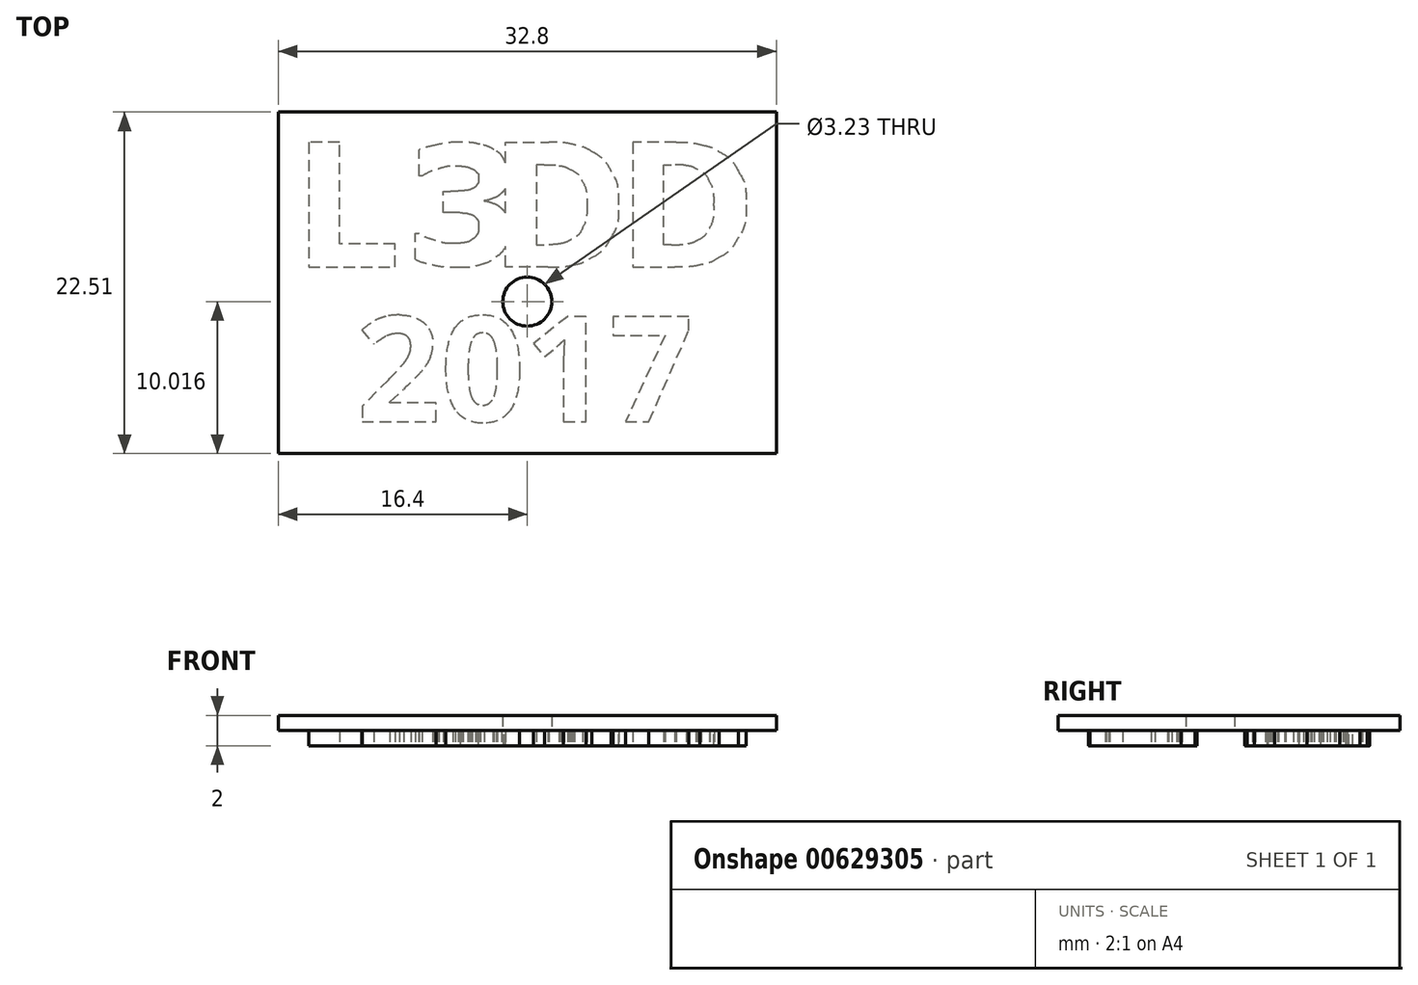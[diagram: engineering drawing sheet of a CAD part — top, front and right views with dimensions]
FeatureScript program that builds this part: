
annotation { "Feature Type Name" : "Feature", "Feature Type Description" : "" }
export const myFeature = defineFeature(function(context is Context, id is Id, definition is map)
    precondition{}
    {
        {
            var Q0;
            Q0=qCreatedBy(makeId("Top.planeOp"),FACE);
            var sketch = newSketch(context, id + "F0", { "sketchPlane" : qUnion([Q0])});
            skText(sketch, "E0", { "text": "2017", "fontName": "OpenSans-Bold.ttf"});
            skFitSpline(sketch, "E1", {"points": [v(-4.44, 4.1) * mm, v(-4.95, 4.1) * mm, v(-5.45, 4.05) * mm, v(-5.95, 3.94) * mm]});
            skFitSpline(sketch, "E2", {"points": [v(-5.95, 3.94) * mm, v(-6.45, 3.84) * mm, v(-6.84, 3.73) * mm, v(-7.13, 3.61) * mm]});
            skFitSpline(sketch, "E3", {"points": [v(-6.94, 1.9) * mm, v(-6.57, 2.11) * mm, v(-6.2, 2.28) * mm, v(-5.8, 2.4) * mm]});
            skFitSpline(sketch, "E4", {"points": [v(-5.8, 2.4) * mm, v(-5.42, 2.5) * mm, v(-5.06, 2.57) * mm, v(-4.73, 2.57) * mm]});
            skFitSpline(sketch, "E5", {"points": [v(-4.73, 2.57) * mm, v(-4.6, 2.57) * mm, v(-4.43, 2.56) * mm, v(-4.25, 2.54) * mm]});
            skFitSpline(sketch, "E6", {"points": [v(-4.25, 2.54) * mm, v(-4.06, 2.51) * mm, v(-3.95, 2.5) * mm, v(-3.76, 2.42) * mm]});
            skFitSpline(sketch, "E7", {"points": [v(-3.76, 2.42) * mm, v(-3.63, 2.36) * mm, v(-3.5, 2.31) * mm, v(-3.42, 2.22) * mm]});
            skFitSpline(sketch, "E8", {"points": [v(-3.42, 2.22) * mm, v(-3.3, 2.12) * mm, v(-3.21, 2.03) * mm, v(-3.21, 1.8) * mm]});
            skFitSpline(sketch, "E9", {"points": [v(-3.21, 1.8) * mm, v(-3.21, 1.48) * mm, v(-3.25, 1.41) * mm, v(-3.33, 1.3) * mm]});
            skFitSpline(sketch, "E10", {"points": [v(-3.33, 1.3) * mm, v(-3.4, 1.2) * mm, v(-3.52, 1.1) * mm, v(-3.68, 1.04) * mm]});
            skFitSpline(sketch, "E11", {"points": [v(-3.68, 1.04) * mm, v(-3.83, 0.97) * mm, v(-4.12, 0.93) * mm, v(-4.34, 0.91) * mm]});
            skFitSpline(sketch, "E12", {"points": [v(-4.34, 0.91) * mm, v(-4.55, 0.9) * mm, v(-4.8, 0.89) * mm, v(-5.07, 0.89) * mm]});
            skLineSegment(sketch, "E13", {"start": v(-7.13, 3.61) * mm, "end": v(-7.13, 1.9) * mm});
            skLineSegment(sketch, "E14", {"start": v(-7.13, 1.9) * mm, "end": v(-6.94, 1.9) * mm});
            skFitSpline(sketch, "E15", {"points": [v(-5.08, -0.52) * mm, v(-4.87, -0.52) * mm, v(-4.65, -0.53) * mm, v(-4.4, -0.53) * mm]});
            skFitSpline(sketch, "E16", {"points": [v(-4.4, -0.53) * mm, v(-4.16, -0.54) * mm, v(-3.95, -0.57) * mm, v(-3.78, -0.62) * mm]});
            skFitSpline(sketch, "E17", {"points": [v(-3.78, -0.62) * mm, v(-3.6, -0.68) * mm, v(-3.47, -0.77) * mm, v(-3.36, -0.9) * mm]});
            skFitSpline(sketch, "E18", {"points": [v(-3.36, -0.9) * mm, v(-3.25, -1.02) * mm, v(-3.2, -1.2) * mm, v(-3.2, -1.42) * mm]});
            skFitSpline(sketch, "E19", {"points": [v(-3.2, -1.42) * mm, v(-3.2, -1.66) * mm, v(-3.24, -1.84) * mm, v(-3.32, -1.97) * mm]});
            skFitSpline(sketch, "E20", {"points": [v(-3.32, -1.97) * mm, v(-3.4, -2.1) * mm, v(-3.5, -2.2) * mm, v(-3.63, -2.29) * mm]});
            skFitSpline(sketch, "E21", {"points": [v(-3.63, -2.29) * mm, v(-3.8, -2.4) * mm, v(-4, -2.47) * mm, v(-4.24, -2.5) * mm]});
            skFitSpline(sketch, "E22", {"points": [v(-4.24, -2.5) * mm, v(-4.48, -2.54) * mm, v(-4.7, -2.56) * mm, v(-4.9, -2.56) * mm]});
            skFitSpline(sketch, "E23", {"points": [v(-4.9, -2.56) * mm, v(-5.26, -2.56) * mm, v(-5.64, -2.49) * mm, v(-6.07, -2.36) * mm]});
            skFitSpline(sketch, "E24", {"points": [v(-6.07, -2.36) * mm, v(-6.49, -2.22) * mm, v(-6.85, -2.06) * mm, v(-7.15, -1.88) * mm]});
            skLineSegment(sketch, "E25", {"start": v(-5.07, 0.89) * mm, "end": v(-5.52, 0.89) * mm});
            skLineSegment(sketch, "E26", {"start": v(-5.52, 0.89) * mm, "end": v(-5.52, -0.52) * mm});
            skLineSegment(sketch, "E27", {"start": v(-5.52, -0.52) * mm, "end": v(-5.08, -0.52) * mm});
            skFitSpline(sketch, "E28", {"points": [v(-7.36, -3.61) * mm, v(-7.07, -3.74) * mm, v(-6.69, -3.85) * mm, v(-6.22, -3.96) * mm]});
            skFitSpline(sketch, "E29", {"points": [v(-6.22, -3.96) * mm, v(-5.75, -4.06) * mm, v(-5.2, -4.1) * mm, v(-4.54, -4.1) * mm]});
            skFitSpline(sketch, "E30", {"points": [v(-4.54, -4.1) * mm, v(-3.96, -4.1) * mm, v(-3.48, -4.05) * mm, v(-3.08, -3.93) * mm]});
            skFitSpline(sketch, "E31", {"points": [v(-3.08, -3.93) * mm, v(-2.68, -3.81) * mm, v(-2.33, -3.64) * mm, v(-2.03, -3.42) * mm]});
            skFitSpline(sketch, "E32", {"points": [v(-2.03, -3.42) * mm, v(-1.77, -3.23) * mm, v(-1.58, -3) * mm, v(-1.43, -2.73) * mm]});
            skLineSegment(sketch, "E33", {"start": v(-7.15, -1.88) * mm, "end": v(-7.36, -1.88) * mm});
            skLineSegment(sketch, "E34", {"start": v(-7.36, -1.88) * mm, "end": v(-7.36, -3.61) * mm});
            skFitSpline(sketch, "E35", {"points": [v(1.35, -4.1) * mm, v(1.98, -4.1) * mm, v(2.52, -4.06) * mm, v(2.98, -3.97) * mm]});
            skFitSpline(sketch, "E36", {"points": [v(2.98, -3.97) * mm, v(3.44, -3.88) * mm, v(3.86, -3.72) * mm, v(4.25, -3.48) * mm]});
            skFitSpline(sketch, "E37", {"points": [v(4.25, -3.48) * mm, v(4.76, -3.17) * mm, v(5.18, -2.73) * mm, v(5.52, -2.15) * mm]});
            skFitSpline(sketch, "E38", {"points": [v(5.52, -2.15) * mm, v(5.85, -1.56) * mm, v(6.02, -0.74) * mm, v(6.02, 0) * mm]});
            skFitSpline(sketch, "E39", {"points": [v(6.02, 0) * mm, v(6.02, 0.76) * mm, v(5.86, 1.58) * mm, v(5.55, 2.14) * mm]});
            skFitSpline(sketch, "E40", {"points": [v(5.55, 2.14) * mm, v(5.24, 2.7) * mm, v(4.81, 3.16) * mm, v(4.27, 3.49) * mm]});
            skFitSpline(sketch, "E41", {"points": [v(4.27, 3.49) * mm, v(3.95, 3.69) * mm, v(3.56, 3.84) * mm, v(3.1, 3.94) * mm]});
            skFitSpline(sketch, "E42", {"points": [v(3.1, 3.94) * mm, v(2.63, 4.05) * mm, v(2.07, 4.1) * mm, v(1.43, 4.1) * mm]});
            skLineSegment(sketch, "E43", {"start": v(-1.43, -2.73) * mm, "end": v(-1.43, -4.1) * mm});
            skLineSegment(sketch, "E44", {"start": v(-1.43, -4.1) * mm, "end": v(1.35, -4.1) * mm});
            skFitSpline(sketch, "E45", {"points": [v(-1.43, 2.75) * mm, v(-1.47, 2.84) * mm, v(-1.51, 2.93) * mm, v(-1.55, 3) * mm]});
            skFitSpline(sketch, "E46", {"points": [v(-1.55, 3) * mm, v(-1.7, 3.25) * mm, v(-1.91, 3.46) * mm, v(-2.2, 3.63) * mm]});
            skFitSpline(sketch, "E47", {"points": [v(-2.2, 3.63) * mm, v(-2.44, 3.78) * mm, v(-2.75, 3.9) * mm, v(-3.13, 3.98) * mm]});
            skFitSpline(sketch, "E48", {"points": [v(-3.13, 3.98) * mm, v(-3.5, 4.07) * mm, v(-3.94, 4.1) * mm, v(-4.44, 4.1) * mm]});
            skLineSegment(sketch, "E49", {"start": v(1.43, 4.1) * mm, "end": v(-1.43, 4.1) * mm});
            skLineSegment(sketch, "E50", {"start": v(-1.43, 4.1) * mm, "end": v(-1.43, 2.75) * mm});
            skFitSpline(sketch, "E51", {"points": [v(1.12, 2.64) * mm, v(1.55, 2.64) * mm, v(1.88, 2.62) * mm, v(2.1, 2.58) * mm]});
            skFitSpline(sketch, "E52", {"points": [v(2.1, 2.58) * mm, v(2.31, 2.54) * mm, v(2.53, 2.47) * mm, v(2.74, 2.37) * mm]});
            skFitSpline(sketch, "E53", {"points": [v(2.74, 2.37) * mm, v(3.15, 2.16) * mm, v(3.45, 1.87) * mm, v(3.63, 1.5) * mm]});
            skFitSpline(sketch, "E54", {"points": [v(3.63, 1.5) * mm, v(3.82, 1.13) * mm, v(3.92, 0.53) * mm, v(3.92, 0) * mm]});
            skFitSpline(sketch, "E55", {"points": [v(3.92, 0) * mm, v(3.92, -0.51) * mm, v(3.83, -1.12) * mm, v(3.66, -1.47) * mm]});
            skFitSpline(sketch, "E56", {"points": [v(3.66, -1.47) * mm, v(3.49, -1.83) * mm, v(3.21, -2.11) * mm, v(2.84, -2.32) * mm]});
            skFitSpline(sketch, "E57", {"points": [v(2.84, -2.32) * mm, v(2.63, -2.44) * mm, v(2.4, -2.52) * mm, v(2.18, -2.57) * mm]});
            skFitSpline(sketch, "E58", {"points": [v(2.18, -2.57) * mm, v(1.95, -2.6) * mm, v(1.6, -2.63) * mm, v(1.12, -2.63) * mm]});
            skLineSegment(sketch, "E59", {"start": v(0.6, 2.64) * mm, "end": v(1.12, 2.64) * mm});
            skLineSegment(sketch, "E60", {"start": v(1.12, -2.63) * mm, "end": v(0.6, -2.63) * mm});
            skLineSegment(sketch, "E61", {"start": v(0.6, -2.63) * mm, "end": v(0.6, 2.64) * mm});
            skFitSpline(sketch, "E62", {"points": [v(-1.43, -0.54) * mm, v(-1.51, -0.43) * mm, v(-1.6, -0.33) * mm, v(-1.7, -0.25) * mm]});
            skFitSpline(sketch, "E63", {"points": [v(-1.7, -0.25) * mm, v(-1.87, -0.1) * mm, v(-2.05, 0) * mm, v(-2.25, 0.08) * mm]});
            skFitSpline(sketch, "E64", {"points": [v(-2.25, 0.08) * mm, v(-2.45, 0.15) * mm, v(-2.65, 0.2) * mm, v(-2.83, 0.23) * mm]});
            skLineSegment(sketch, "E65", {"start": v(-1.43, 1.06) * mm, "end": v(-1.43, -0.54) * mm});
            skFitSpline(sketch, "E66", {"points": [v(-2.83, 0.3) * mm, v(-2.65, 0.32) * mm, v(-2.45, 0.37) * mm, v(-2.25, 0.45) * mm]});
            skFitSpline(sketch, "E67", {"points": [v(-2.25, 0.45) * mm, v(-2.05, 0.52) * mm, v(-1.87, 0.63) * mm, v(-1.7, 0.77) * mm]});
            skFitSpline(sketch, "E68", {"points": [v(-1.7, 0.77) * mm, v(-1.6, 0.86) * mm, v(-1.51, 0.96) * mm, v(-1.43, 1.06) * mm]});
            skLineSegment(sketch, "E69", {"start": v(-2.83, 0.23) * mm, "end": v(-2.83, 0.3) * mm});
            skFitSpline(sketch, "E70", {"points": [v(14.4, 0) * mm, v(14.4, -0.74) * mm, v(14.23, -1.56) * mm, v(13.9, -2.15) * mm]});
            skFitSpline(sketch, "E71", {"points": [v(13.9, -2.15) * mm, v(13.56, -2.73) * mm, v(13.13, -3.17) * mm, v(12.62, -3.48) * mm]});
            skFitSpline(sketch, "E72", {"points": [v(12.62, -3.48) * mm, v(12.24, -3.72) * mm, v(11.81, -3.88) * mm, v(11.36, -3.97) * mm]});
            skFitSpline(sketch, "E73", {"points": [v(11.36, -3.97) * mm, v(10.9, -4.06) * mm, v(10.35, -4.1) * mm, v(9.72, -4.1) * mm]});
            skFitSpline(sketch, "E74", {"points": [v(9.8, 4.1) * mm, v(10.45, 4.1) * mm, v(11, 4.05) * mm, v(11.47, 3.94) * mm]});
            skFitSpline(sketch, "E75", {"points": [v(11.47, 3.94) * mm, v(11.93, 3.84) * mm, v(12.33, 3.69) * mm, v(12.64, 3.49) * mm]});
            skFitSpline(sketch, "E76", {"points": [v(12.64, 3.49) * mm, v(13.19, 3.16) * mm, v(13.61, 2.7) * mm, v(13.93, 2.14) * mm]});
            skFitSpline(sketch, "E77", {"points": [v(13.93, 2.14) * mm, v(14.24, 1.58) * mm, v(14.4, 0.76) * mm, v(14.4, 0) * mm]});
            skLineSegment(sketch, "E78", {"start": v(9.72, -4.1) * mm, "end": v(6.94, -4.1) * mm});
            skLineSegment(sketch, "E79", {"start": v(6.94, -4.1) * mm, "end": v(6.94, 4.1) * mm});
            skLineSegment(sketch, "E80", {"start": v(6.94, 4.1) * mm, "end": v(9.8, 4.1) * mm});
            skFitSpline(sketch, "E81", {"points": [v(12.3, 0) * mm, v(12.3, 0.53) * mm, v(12.2, 1.13) * mm, v(12, 1.5) * mm]});
            skFitSpline(sketch, "E82", {"points": [v(12, 1.5) * mm, v(11.82, 1.87) * mm, v(11.52, 2.16) * mm, v(11.11, 2.37) * mm]});
            skFitSpline(sketch, "E83", {"points": [v(11.11, 2.37) * mm, v(10.9, 2.47) * mm, v(10.69, 2.54) * mm, v(10.47, 2.58) * mm]});
            skFitSpline(sketch, "E84", {"points": [v(10.47, 2.58) * mm, v(10.26, 2.62) * mm, v(9.93, 2.64) * mm, v(9.5, 2.64) * mm]});
            skFitSpline(sketch, "E85", {"points": [v(9.5, -2.63) * mm, v(9.97, -2.63) * mm, v(10.33, -2.6) * mm, v(10.56, -2.57) * mm]});
            skFitSpline(sketch, "E86", {"points": [v(10.56, -2.57) * mm, v(10.78, -2.52) * mm, v(11, -2.44) * mm, v(11.22, -2.32) * mm]});
            skFitSpline(sketch, "E87", {"points": [v(11.22, -2.32) * mm, v(11.59, -2.11) * mm, v(11.86, -1.83) * mm, v(12.03, -1.47) * mm]});
            skFitSpline(sketch, "E88", {"points": [v(12.03, -1.47) * mm, v(12.2, -1.12) * mm, v(12.3, -0.51) * mm, v(12.3, 0) * mm]});
            skLineSegment(sketch, "E89", {"start": v(9.5, 2.64) * mm, "end": v(8.98, 2.64) * mm});
            skLineSegment(sketch, "E90", {"start": v(8.98, 2.64) * mm, "end": v(8.98, -2.63) * mm});
            skLineSegment(sketch, "E91", {"start": v(8.98, -2.63) * mm, "end": v(9.5, -2.63) * mm});
            skLineSegment(sketch, "E92", {"start": v(-8.7, -4.1) * mm, "end": v(-14.4, -4.1) * mm});
            skLineSegment(sketch, "E93", {"start": v(-14.4, -4.1) * mm, "end": v(-14.4, 4.1) * mm});
            skLineSegment(sketch, "E94", {"start": v(-14.4, 4.1) * mm, "end": v(-12.36, 4.1) * mm});
            skLineSegment(sketch, "E95", {"start": v(-12.36, 4.1) * mm, "end": v(-12.36, -2.58) * mm});
            skLineSegment(sketch, "E96", {"start": v(-12.36, -2.58) * mm, "end": v(-8.7, -2.58) * mm});
            skLineSegment(sketch, "E97", {"start": v(-8.7, -2.58) * mm, "end": v(-8.7, -4.1) * mm});
            const initialGuessF0  = {"E0": [-0.01126, -0.0143, 1, 0, 0.007]};
            skSetInitialGuess(sketch, initialGuessF0);
            skSolve(sketch);
        }
        {
            var Q0;
            Q0 = qSketchRegion(id + "F0", true);
            extrude(context, id + "F1", {"entities" : qUnion([Q0]), "endBound" : BoundingType.SYMMETRIC, "depth" : 2 * mm, "offsetDistance" : 25 * mm});
        }
        {
            var Q0;
            Q0=qCreatedBy(makeId("Top.planeOp"),FACE);
            var sketch = newSketch(context, id + "F2", { "sketchPlane" : qUnion([Q0])});
            skLineSegment(sketch, "E98.bottom", {"start": v(-16.4, 6.1) * mm, "end": v(16.4, 6.1) * mm});
            skLineSegment(sketch, "E98.top", {"start": v(-16.4, -16.4) * mm, "end": v(16.4, -16.4) * mm});
            skLineSegment(sketch, "E98.left", {"start": v(-16.4, 6.1) * mm, "end": v(-16.4, -16.4) * mm});
            skLineSegment(sketch, "E98.right", {"start": v(16.4, 6.1) * mm, "end": v(16.4, -16.4) * mm});
            skSolve(sketch);
        }
        {
            var Q0;
            Q0=makeQuery(id+"F2.imprint","IMPRINT",FACE,{"disambiguationData":[TD([[makeQuery(id+"F2.imprint","IMPRINT",EDGE,{"derivedFrom":sQuery(id+"F2.wireOp",EDGE,"E98.bottom")}),-1.0]])]});
            extrude(context, id + "F3", {"entities" : qUnion([Q0]), "depth" : 1 * mm, "offsetDistance" : 25 * mm});
        }
        {
            var Q0;
            Q0=makeQuery(id+"F3.opExtrude","SWEPT_BODY",BODY,{"disambiguationData":[OSD([sQuery(id+"F2.wireOp",EDGE,"E98.bottom"),sQuery(id+"F2.wireOp",EDGE,"E98.top"),sQuery(id+"F2.wireOp",EDGE,"E98.left"),sQuery(id+"F2.wireOp",EDGE,"E98.right")])]});
            var Q1;
            Q1=makeQuery(id+"F1.opExtrude","SWEPT_BODY",BODY,{"disambiguationData":[OSD([sQuery(id+"F0.wireOp",EDGE,"E0.sketch_text.stroke-0"),sQuery(id+"F0.wireOp",EDGE,"E0.sketch_text.stroke-1"),sQuery(id+"F0.wireOp",EDGE,"E0.sketch_text.stroke-2"),sQuery(id+"F0.wireOp",EDGE,"E0.sketch_text.stroke-3"),sQuery(id+"F0.wireOp",EDGE,"E0.sketch_text.stroke-4"),sQuery(id+"F0.wireOp",EDGE,"E0.sketch_text.stroke-5"),sQuery(id+"F0.wireOp",EDGE,"E0.sketch_text.stroke-6"),sQuery(id+"F0.wireOp",EDGE,"E0.sketch_text.stroke-7"),sQuery(id+"F0.wireOp",EDGE,"E0.sketch_text.stroke-8"),sQuery(id+"F0.wireOp",EDGE,"E0.sketch_text.stroke-9"),sQuery(id+"F0.wireOp",EDGE,"E0.sketch_text.stroke-10"),sQuery(id+"F0.wireOp",EDGE,"E0.sketch_text.stroke-11"),sQuery(id+"F0.wireOp",EDGE,"E0.sketch_text.stroke-12"),sQuery(id+"F0.wireOp",EDGE,"E0.sketch_text.stroke-13"),sQuery(id+"F0.wireOp",EDGE,"E0.sketch_text.stroke-14"),sQuery(id+"F0.wireOp",EDGE,"E0.sketch_text.stroke-15"),sQuery(id+"F0.wireOp",EDGE,"E0.sketch_text.stroke-16"),sQuery(id+"F0.wireOp",EDGE,"E0.sketch_text.stroke-17"),sQuery(id+"F0.wireOp",EDGE,"E0.sketch_text.stroke-18"),sQuery(id+"F0.wireOp",EDGE,"E0.sketch_text.stroke-19"),sQuery(id+"F0.wireOp",EDGE,"E0.sketch_text.stroke-20"),sQuery(id+"F0.wireOp",EDGE,"E0.sketch_text.stroke-21"),sQuery(id+"F0.wireOp",EDGE,"E0.sketch_text.stroke-22"),sQuery(id+"F0.wireOp",EDGE,"E0.sketch_text.stroke-23")])]});
            var Q2;
            Q2=makeQuery(id+"F1.opExtrude","SWEPT_BODY",BODY,{"disambiguationData":[OSD([sQuery(id+"F0.wireOp",EDGE,"E0.sketch_text.stroke-24"),sQuery(id+"F0.wireOp",EDGE,"E0.sketch_text.stroke-25"),sQuery(id+"F0.wireOp",EDGE,"E0.sketch_text.stroke-26"),sQuery(id+"F0.wireOp",EDGE,"E0.sketch_text.stroke-27"),sQuery(id+"F0.wireOp",EDGE,"E0.sketch_text.stroke-28"),sQuery(id+"F0.wireOp",EDGE,"E0.sketch_text.stroke-29"),sQuery(id+"F0.wireOp",EDGE,"E0.sketch_text.stroke-30"),sQuery(id+"F0.wireOp",EDGE,"E0.sketch_text.stroke-31"),sQuery(id+"F0.wireOp",EDGE,"E0.sketch_text.stroke-32"),sQuery(id+"F0.wireOp",EDGE,"E0.sketch_text.stroke-33"),sQuery(id+"F0.wireOp",EDGE,"E0.sketch_text.stroke-34"),sQuery(id+"F0.wireOp",EDGE,"E0.sketch_text.stroke-35"),sQuery(id+"F0.wireOp",EDGE,"E0.sketch_text.stroke-36"),sQuery(id+"F0.wireOp",EDGE,"E0.sketch_text.stroke-37"),sQuery(id+"F0.wireOp",EDGE,"E0.sketch_text.stroke-38"),sQuery(id+"F0.wireOp",EDGE,"E0.sketch_text.stroke-39")])]});
            var Q3;
            Q3=makeQuery(id+"F1.opExtrude","SWEPT_BODY",BODY,{"disambiguationData":[OSD([sQuery(id+"F0.wireOp",EDGE,"E0.sketch_text.stroke-40"),sQuery(id+"F0.wireOp",EDGE,"E0.sketch_text.stroke-41"),sQuery(id+"F0.wireOp",EDGE,"E0.sketch_text.stroke-42"),sQuery(id+"F0.wireOp",EDGE,"E0.sketch_text.stroke-43"),sQuery(id+"F0.wireOp",EDGE,"E0.sketch_text.stroke-44"),sQuery(id+"F0.wireOp",EDGE,"E0.sketch_text.stroke-45"),sQuery(id+"F0.wireOp",EDGE,"E0.sketch_text.stroke-46"),sQuery(id+"F0.wireOp",EDGE,"E0.sketch_text.stroke-47"),sQuery(id+"F0.wireOp",EDGE,"E0.sketch_text.stroke-48"),sQuery(id+"F0.wireOp",EDGE,"E0.sketch_text.stroke-49")])]});
            var Q4;
            Q4=makeQuery(id+"F1.opExtrude","SWEPT_BODY",BODY,{"disambiguationData":[OSD([sQuery(id+"F0.wireOp",EDGE,"E0.sketch_text.stroke-50"),sQuery(id+"F0.wireOp",EDGE,"E0.sketch_text.stroke-51"),sQuery(id+"F0.wireOp",EDGE,"E0.sketch_text.stroke-52"),sQuery(id+"F0.wireOp",EDGE,"E0.sketch_text.stroke-53"),sQuery(id+"F0.wireOp",EDGE,"E0.sketch_text.stroke-54"),sQuery(id+"F0.wireOp",EDGE,"E0.sketch_text.stroke-55"),sQuery(id+"F0.wireOp",EDGE,"E0.sketch_text.stroke-56")])]});
            var Q5;
            Q5=makeQuery(id+"F1.opExtrude","SWEPT_BODY",BODY,{"disambiguationData":[OSD([sQuery(id+"F0.wireOp",EDGE,"E1"),sQuery(id+"F0.wireOp",EDGE,"E2"),sQuery(id+"F0.wireOp",EDGE,"E3"),sQuery(id+"F0.wireOp",EDGE,"E4"),sQuery(id+"F0.wireOp",EDGE,"E5"),sQuery(id+"F0.wireOp",EDGE,"E6"),sQuery(id+"F0.wireOp",EDGE,"E7"),sQuery(id+"F0.wireOp",EDGE,"E8"),sQuery(id+"F0.wireOp",EDGE,"E9"),sQuery(id+"F0.wireOp",EDGE,"E10"),sQuery(id+"F0.wireOp",EDGE,"E11"),sQuery(id+"F0.wireOp",EDGE,"E12"),sQuery(id+"F0.wireOp",EDGE,"E13"),sQuery(id+"F0.wireOp",EDGE,"E14"),sQuery(id+"F0.wireOp",EDGE,"E15"),sQuery(id+"F0.wireOp",EDGE,"E16"),sQuery(id+"F0.wireOp",EDGE,"E17"),sQuery(id+"F0.wireOp",EDGE,"E18"),sQuery(id+"F0.wireOp",EDGE,"E19"),sQuery(id+"F0.wireOp",EDGE,"E20"),sQuery(id+"F0.wireOp",EDGE,"E21"),sQuery(id+"F0.wireOp",EDGE,"E22"),sQuery(id+"F0.wireOp",EDGE,"E23"),sQuery(id+"F0.wireOp",EDGE,"E24"),sQuery(id+"F0.wireOp",EDGE,"E25"),sQuery(id+"F0.wireOp",EDGE,"E26"),sQuery(id+"F0.wireOp",EDGE,"E27"),sQuery(id+"F0.wireOp",EDGE,"E28"),sQuery(id+"F0.wireOp",EDGE,"E29"),sQuery(id+"F0.wireOp",EDGE,"E30"),sQuery(id+"F0.wireOp",EDGE,"E31"),sQuery(id+"F0.wireOp",EDGE,"E32"),sQuery(id+"F0.wireOp",EDGE,"E33"),sQuery(id+"F0.wireOp",EDGE,"E34"),sQuery(id+"F0.wireOp",EDGE,"E35"),sQuery(id+"F0.wireOp",EDGE,"E36"),sQuery(id+"F0.wireOp",EDGE,"E37"),sQuery(id+"F0.wireOp",EDGE,"E38"),sQuery(id+"F0.wireOp",EDGE,"E39"),sQuery(id+"F0.wireOp",EDGE,"E40"),sQuery(id+"F0.wireOp",EDGE,"E41"),sQuery(id+"F0.wireOp",EDGE,"E42"),sQuery(id+"F0.wireOp",EDGE,"E43"),sQuery(id+"F0.wireOp",EDGE,"E44"),sQuery(id+"F0.wireOp",EDGE,"E45"),sQuery(id+"F0.wireOp",EDGE,"E46"),sQuery(id+"F0.wireOp",EDGE,"E47"),sQuery(id+"F0.wireOp",EDGE,"E48"),sQuery(id+"F0.wireOp",EDGE,"E49"),sQuery(id+"F0.wireOp",EDGE,"E50"),sQuery(id+"F0.wireOp",EDGE,"E51"),sQuery(id+"F0.wireOp",EDGE,"E52"),sQuery(id+"F0.wireOp",EDGE,"E53"),sQuery(id+"F0.wireOp",EDGE,"E54"),sQuery(id+"F0.wireOp",EDGE,"E55"),sQuery(id+"F0.wireOp",EDGE,"E56"),sQuery(id+"F0.wireOp",EDGE,"E57"),sQuery(id+"F0.wireOp",EDGE,"E58"),sQuery(id+"F0.wireOp",EDGE,"E59"),sQuery(id+"F0.wireOp",EDGE,"E60"),sQuery(id+"F0.wireOp",EDGE,"E61"),sQuery(id+"F0.wireOp",EDGE,"E62"),sQuery(id+"F0.wireOp",EDGE,"E63"),sQuery(id+"F0.wireOp",EDGE,"E64"),sQuery(id+"F0.wireOp",EDGE,"E65"),sQuery(id+"F0.wireOp",EDGE,"E66"),sQuery(id+"F0.wireOp",EDGE,"E67"),sQuery(id+"F0.wireOp",EDGE,"E68"),sQuery(id+"F0.wireOp",EDGE,"E69")])]});
            var Q6;
            Q6=makeQuery(id+"F1.opExtrude","SWEPT_BODY",BODY,{"disambiguationData":[OSD([sQuery(id+"F0.wireOp",EDGE,"E70"),sQuery(id+"F0.wireOp",EDGE,"E71"),sQuery(id+"F0.wireOp",EDGE,"E72"),sQuery(id+"F0.wireOp",EDGE,"E73"),sQuery(id+"F0.wireOp",EDGE,"E74"),sQuery(id+"F0.wireOp",EDGE,"E75"),sQuery(id+"F0.wireOp",EDGE,"E76"),sQuery(id+"F0.wireOp",EDGE,"E77"),sQuery(id+"F0.wireOp",EDGE,"E78"),sQuery(id+"F0.wireOp",EDGE,"E79"),sQuery(id+"F0.wireOp",EDGE,"E80"),sQuery(id+"F0.wireOp",EDGE,"E81"),sQuery(id+"F0.wireOp",EDGE,"E82"),sQuery(id+"F0.wireOp",EDGE,"E83"),sQuery(id+"F0.wireOp",EDGE,"E84"),sQuery(id+"F0.wireOp",EDGE,"E85"),sQuery(id+"F0.wireOp",EDGE,"E86"),sQuery(id+"F0.wireOp",EDGE,"E87"),sQuery(id+"F0.wireOp",EDGE,"E88"),sQuery(id+"F0.wireOp",EDGE,"E89"),sQuery(id+"F0.wireOp",EDGE,"E90"),sQuery(id+"F0.wireOp",EDGE,"E91")])]});
            var Q7;
            Q7=makeQuery(id+"F1.opExtrude","SWEPT_BODY",BODY,{"disambiguationData":[OSD([sQuery(id+"F0.wireOp",EDGE,"E92"),sQuery(id+"F0.wireOp",EDGE,"E93"),sQuery(id+"F0.wireOp",EDGE,"E94"),sQuery(id+"F0.wireOp",EDGE,"E95"),sQuery(id+"F0.wireOp",EDGE,"E96"),sQuery(id+"F0.wireOp",EDGE,"E97")])]});
            booleanBodies(context, id + "F4", {"operationType" : BooleanOperationType.UNION, "tools" : qUnion([Q0, Q1, Q2, Q3, Q4, Q5, Q6, Q7])});
        }
        {
            var Q0;
            {var subQ0=sQuery(id+"F2.wireOp",EDGE,"E98.right");var subQ1=sQuery(id+"F2.wireOp",EDGE,"E98.bottom");var subQ2=sQuery(id+"F2.wireOp",EDGE,"E98.top");var subQ3=sQuery(id+"F2.wireOp",EDGE,"E98.left");Q0=makeQuery(id+"F4.opBoolean","SPLIT",FACE,{"disambiguationData":[TD([makeQuery(id+"F1.opExtrude","SWEPT_FACE",FACE,{"disambiguationData":[OSD([sQuery(id+"F0.wireOp",EDGE,"E0.sketch_text.stroke-0")])]})])],"derivedFrom":makeQuery(id+"F3.opExtrude","CAP_FACE",FACE,{"disambiguationData":[OSD([subQ1,subQ2,subQ3,subQ0])],"isStart":true})});}
            var sketch = newSketch(context, id + "F5", { "sketchPlane" : qUnion([Q0])});
            skCircle(sketch, "E99", {"center": v(0, 6.38) * mm, "radius": 1.62 * mm});
            skSolve(sketch);
        }
        {
            var Q0;
            Q0 = qSketchRegion(id + "F5", true);
            extrude(context, id + "F6", {"entities" : qUnion([Q0]), "operationType" : NewBodyOperationType.REMOVE, "endBound" : BoundingType.THROUGH_ALL, "oppositeDirection" : true, "depth" : 25 * mm, "offsetDistance" : 25 * mm});
        }
    });
